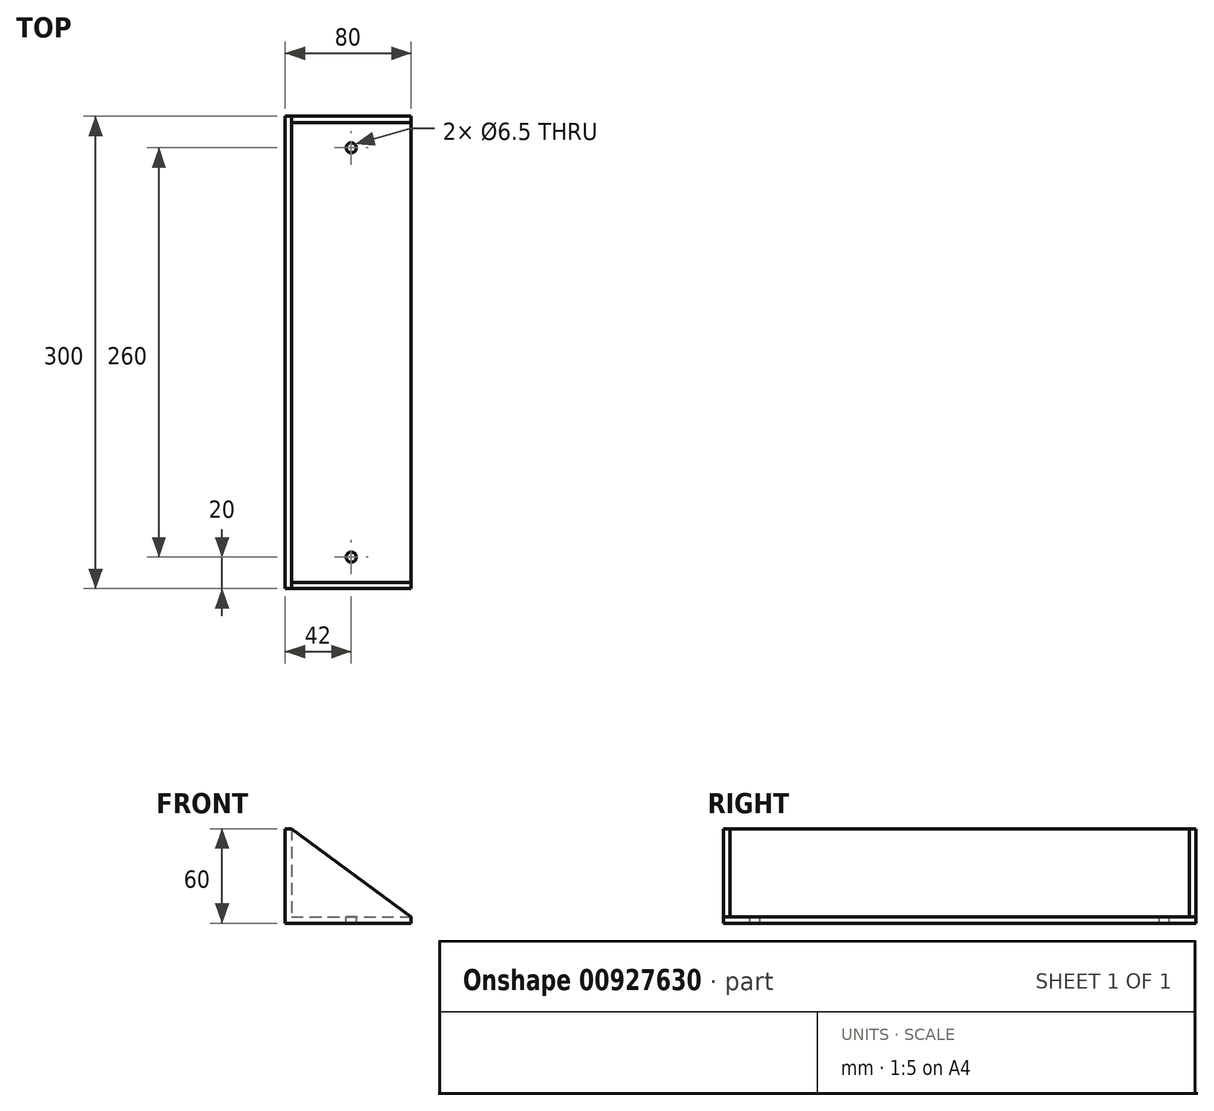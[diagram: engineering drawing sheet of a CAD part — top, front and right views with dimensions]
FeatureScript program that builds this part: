
annotation { "Feature Type Name" : "Feature", "Feature Type Description" : "" }
export const myFeature = defineFeature(function(context is Context, id is Id, definition is map)
    precondition{}
    {
        {
            var Q0;
            Q0=qCreatedBy(makeId("Front.planeOp"),FACE);
            var sketch = newSketch(context, id + "F0", { "sketchPlane" : qUnion([Q0])});
            skLineSegment(sketch, "E0", {"start": v(0, 0) * mm, "end": v(80, 0) * mm});
            skLineSegment(sketch, "E1", {"start": v(0, 0) * mm, "end": v(0, 60) * mm});
            skLineSegment(sketch, "E2.0", {"start": v(4, 4) * mm, "end": v(4, 60) * mm});
            skLineSegment(sketch, "E2.1", {"start": v(4, 4) * mm, "end": v(80, 4) * mm});
            skLineSegment(sketch, "E3", {"start": v(0, 60) * mm, "end": v(4, 60) * mm});
            skLineSegment(sketch, "E4", {"start": v(80, 4) * mm, "end": v(80, 0) * mm});
            skSolve(sketch);
        }
        {
            var Q0;
            Q0 = qSketchRegion(id + "F0", true);
            extrude(context, id + "F1", {"entities" : qUnion([Q0]), "depth" : 300 * mm, "offsetDistance" : 25 * mm});
        }
        {
            var Q0;
            Q0=makeQuery(id+"F1.opExtrude","SWEPT_FACE",FACE,{"disambiguationData":[OSD([sQuery(id+"F0.wireOp",EDGE,"E2.1")])]});
            var sketch = newSketch(context, id + "F2", { "sketchPlane" : qUnion([Q0])});
            skLineSegment(sketch, "E5", {"start": v(42, 26.14) * mm, "end": v(42, -306.78) * mm, "construction": true});
            skPoint(sketch, "E5.startSnap0", {"position": v(42, 0) * mm});
            skPoint(sketch, "E5.endSnap0", {"position": v(42, -300) * mm});
            skCircle(sketch, "E6", {"center": v(42, -20) * mm, "radius": 3.25 * mm});
            skLineSegment(sketch, "E7", {"start": v(91.95, -150) * mm, "end": v(-60.36, -150) * mm, "construction": true});
            skPoint(sketch, "E7.startSnap0", {"position": v(80, -150) * mm});
            skCircle(sketch, "E8.MirrorC", {"center": v(42, -280) * mm, "radius": 3.25 * mm});
            skSolve(sketch);
        }
        {
            var Q0;
            Q0 = qSketchRegion(id + "F2", true);
            extrude(context, id + "F3", {"entities" : qUnion([Q0]), "operationType" : NewBodyOperationType.REMOVE, "oppositeDirection" : true, "depth" : 25 * mm, "offsetDistance" : 25 * mm});
        }
        {
            var Q0;
            Q0=qCreatedBy(makeId("Front.planeOp"),FACE);
            var sketch = newSketch(context, id + "F4", { "sketchPlane" : qUnion([Q0])});
            skLineSegment(sketch, "E9", {"start": v(4, 60) * mm, "end": v(80, 4) * mm});
            skLineSegment(sketch, "E10", {"start": v(80, 4) * mm, "end": v(4, 4) * mm});
            skLineSegment(sketch, "E11", {"start": v(4, 4) * mm, "end": v(4, 60) * mm});
            skSolve(sketch);
        }
        {
            var Q0;
            Q0 = qSketchRegion(id + "F4", true);
            extrude(context, id + "F5", {"entities" : qUnion([Q0]), "operationType" : NewBodyOperationType.ADD, "depth" : 4 * mm, "offsetDistance" : 25 * mm});
        }
        {
            var Q0;
            Q0=qCreatedBy(makeId("Front.planeOp"),FACE);
            cPlane(context, id + "F6", {"entities" : qUnion([Q0]), "cplaneType" : CPlaneType.OFFSET, "offset" : 300 * mm, "width" : 150 * mm, "height" : 150 * mm});
        }
        {
            var Q0;
            Q0=qCreatedBy(id+"F6.planeOp",FACE);
            var sketch = newSketch(context, id + "F7", { "sketchPlane" : qUnion([Q0])});
            skLineSegment(sketch, "E12", {"start": v(4, 60) * mm, "end": v(4, 4) * mm});
            skLineSegment(sketch, "E13", {"start": v(4, 4) * mm, "end": v(80, 4) * mm});
            skLineSegment(sketch, "E14", {"start": v(80, 4) * mm, "end": v(4, 60) * mm});
            skSolve(sketch);
        }
        {
            var Q0;
            Q0 = qSketchRegion(id + "F7", true);
            extrude(context, id + "F8", {"entities" : qUnion([Q0]), "operationType" : NewBodyOperationType.ADD, "oppositeDirection" : true, "depth" : 4 * mm, "offsetDistance" : 25 * mm});
        }
    });
